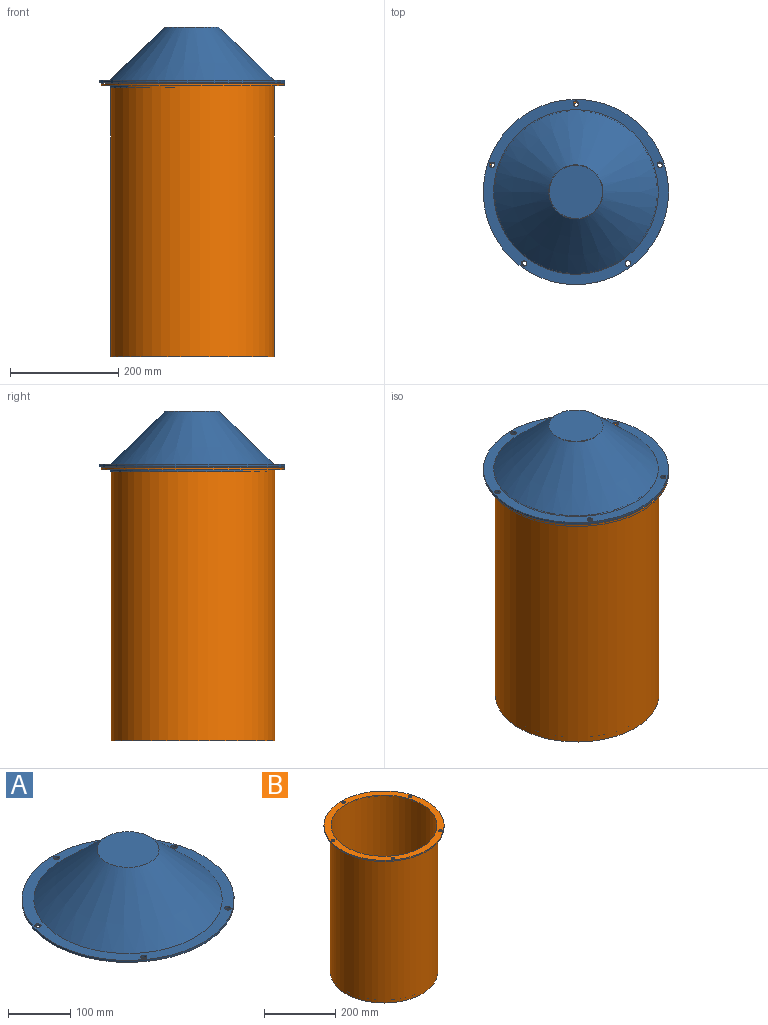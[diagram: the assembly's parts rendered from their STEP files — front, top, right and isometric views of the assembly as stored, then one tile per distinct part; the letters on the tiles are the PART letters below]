
ASSEMBLY  parts=2 mates=1
PART A: 16 faces, bbox 342x342x112 mm
  f0: plane 298x298mm, normal (0,0,1), area 933.1mm2, adj f1,f14
  f1: cylinder r=148mm len=296mm, axis (0,0,-1), area 13018.8mm2, adj f0,f11
  f2: cylinder r=171mm len=342mm, axis (0,0,-1), area 4297.7mm2, adj f3,f4
  f3: plane 342x342mm, normal (0,0,1), area 18997mm2, adj f2,f5,f6,f7,f8,f9,f13
  f4: plane 342x342mm, normal (0,0,-1), area 19839.2mm2, adj f2,f5,f6,f7,f8,f9,f10
  f5: cylinder r=5mm len=10mm, axis (0,0,1), area 125.7mm2, adj f3,f4
  f6: cylinder r=5mm len=10mm, axis (0,0,1), area 125.7mm2, adj f3,f4
  f7: cylinder r=5mm len=10mm, axis (0,0,1), area 125.7mm2, adj f3,f4
  f8: cylinder r=5mm len=10mm, axis (0,0,1), area 125.7mm2, adj f3,f4
  f9: cylinder r=5mm len=10mm, axis (0,0,1), area 125.7mm2, adj f3,f4
  f10: cylinder r=151mm len=302mm, axis (0,0,1), area 9487.6mm2, adj f4,f11
  f11: plane 302x302mm, normal (0,0,-1), area 2818mm2, adj f1,f10
  f12: plane 100x100mm, normal (0,0,1), area 7854mm2, adj f13
  f13: cone r=151.89mm half-angle=46.1deg, axis (0,0,-1), area 89660.5mm2, adj f3,f12
  f14: cone r=149mm half-angle=46.1deg, axis (0,0,-1), area 86225mm2, adj f0,f15
  f15: plane 98.39x98.39mm, normal (0,0,-1), area 7602.9mm2, adj f14
PART B: 12 faces, bbox 338x338x504 mm
  f0: cylinder r=149mm len=494mm, axis (0,0,1), area 462480.1mm2, adj f1,f3
  f1: plane 298x298mm, normal (0,0,1), area 69746.5mm2, adj f0
  f2: cylinder r=169mm len=338mm, axis (0,0,-1), area 4247.4mm2, adj f3,f4
  f3: plane 338x338mm, normal (0,0,1), area 19587.8mm2, adj f0,f2,f7,f8,f9,f10,f11
  f4: plane 338x338mm, normal (0,0,-1), area 17702.9mm2, adj f2,f6,f7,f8,f9,f10,f11
  f5: plane 302x302mm, normal (0,0,-1), area 71631.5mm2, adj f6
  f6: cylinder r=151mm len=500mm, axis (0,0,-1), area 474380.5mm2, adj f4,f5
  f7: cylinder r=5mm len=10mm, axis (0,0,1), area 125.7mm2, adj f3,f4
  f8: cylinder r=5mm len=10mm, axis (0,0,1), area 125.7mm2, adj f3,f4
  f9: cylinder r=5mm len=10mm, axis (0,0,1), area 125.7mm2, adj f3,f4
  f10: cylinder r=5mm len=10mm, axis (0,0,1), area 125.7mm2, adj f3,f4
  f11: cylinder r=5mm len=10mm, axis (0,0,1), area 125.7mm2, adj f3,f4
PLACE A t=(68.53,336.14,465.17)mm
PLACE B t=(69.71,334.52,-40.93)mm
MATE slider B.f8 <-> A.f6  axis (0,0,1) through (164.34,204.27,463.07)mm
